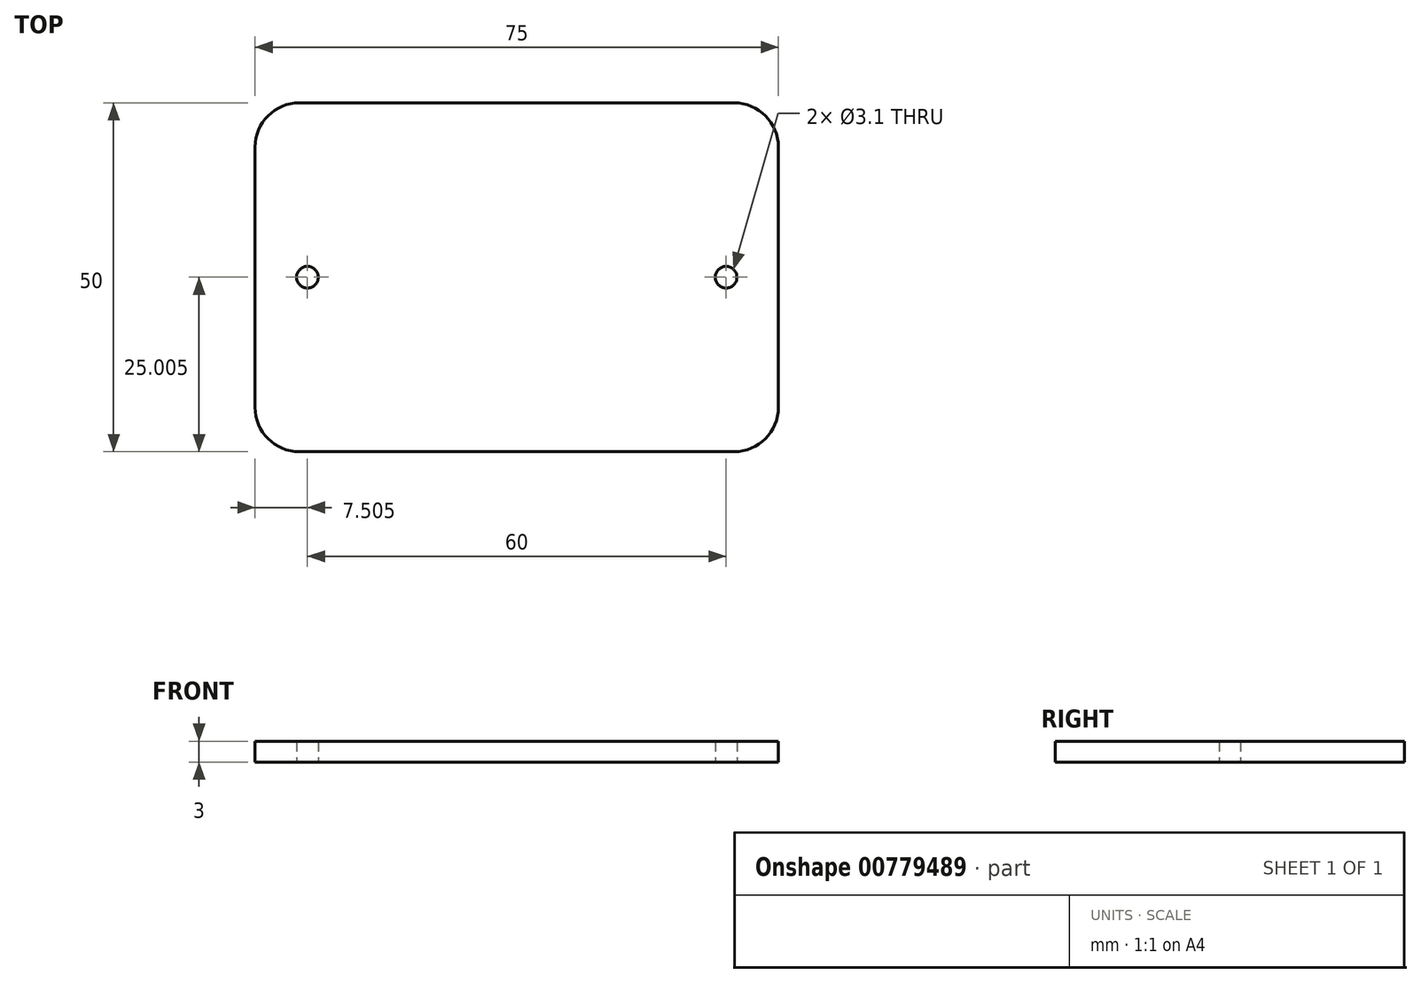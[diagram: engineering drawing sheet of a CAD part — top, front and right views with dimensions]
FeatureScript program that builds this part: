
annotation { "Feature Type Name" : "Feature", "Feature Type Description" : "" }
export const myFeature = defineFeature(function(context is Context, id is Id, definition is map)
    precondition{}
    {
        {
            var Q0;
            Q0=qCreatedBy(makeId("Top.planeOp"),FACE);
            var sketch = newSketch(context, id + "F0", { "sketchPlane" : qUnion([Q0])});
            skLineSegment(sketch, "E0.bottom", {"start": v(-31.92, 31.55) * mm, "end": v(30.38, 31.55) * mm});
            skLineSegment(sketch, "E0.top", {"start": v(-31.92, -18.45) * mm, "end": v(30.38, -18.45) * mm});
            skLineSegment(sketch, "E0.left", {"start": v(-38.27, 25.2) * mm, "end": v(-38.27, -12.1) * mm});
            skLineSegment(sketch, "E0.right", {"start": v(36.73, 25.2) * mm, "end": v(36.73, -12.1) * mm});
            skCircle(sketch, "E1", {"center": v(-30.77, 6.55) * mm, "radius": 1.55 * mm});
            skCircle(sketch, "E2", {"center": v(29.23, 6.55) * mm, "radius": 1.55 * mm});
            skPoint(sketch, "E3", {"position": v(-38.27, 6.55) * mm});
            skPoint(sketch, "E4", {"position": v(36.73, 6.55) * mm});
            skLineSegment(sketch, "E5", {"start": v(-38.27, 6.55) * mm, "end": v(-30.77, 6.55) * mm, "construction": true});
            skLineSegment(sketch, "E6", {"start": v(29.23, 6.55) * mm, "end": v(36.73, 6.55) * mm, "construction": true});
            skPoint(sketch, "E7.visualSharp", {"position": v(-38.27, 31.55) * mm});
            skArc(sketch, "E7.filletArc", {"start": v(-31.92, 31.55) * mm, "mid": v(-36.4, 29.7) * mm, "end": v(-38.27, 25.2) * mm});
            skPoint(sketch, "E8.visualSharp", {"position": v(36.73, 31.55) * mm});
            skArc(sketch, "E8.filletArc", {"start": v(36.73, 25.2) * mm, "mid": v(34.88, 29.7) * mm, "end": v(30.38, 31.55) * mm});
            skPoint(sketch, "E9.visualSharp", {"position": v(36.73, -18.45) * mm});
            skArc(sketch, "E9.filletArc", {"start": v(30.38, -18.45) * mm, "mid": v(34.88, -16.59) * mm, "end": v(36.73, -12.1) * mm});
            skPoint(sketch, "E10.visualSharp", {"position": v(-38.27, -18.45) * mm});
            skArc(sketch, "E10.filletArc", {"start": v(-38.27, -12.1) * mm, "mid": v(-36.4, -16.59) * mm, "end": v(-31.92, -18.45) * mm});
            skSolve(sketch);
        }
        {
            var Q0;
            Q0=makeQuery(id+"F0.imprint","IMPRINT",FACE,{"disambiguationData":[TD([[makeQuery(id+"F0.imprint","IMPRINT",EDGE,{"derivedFrom":sQuery(id+"F0.wireOp",EDGE,"E0.bottom")}),-1.0]])]});
            extrude(context, id + "F1", {"entities" : qUnion([Q0]), "depth" : 3 * mm, "offsetDistance" : 25.4 * mm});
        }
    });
